# Revit family: Shower-Valves_and_Controls-KOHLER-Rite-Temp-K-8300
name_source: partatom
category: Plumbing Fixtures
revit_build: Autodesk Revit 2015 (Build: 20140606_1530(x64)
units: mm (PartAtom-declared; Revit-internal decimal feet)

## types (5) — shared parameters
ADA = No
Assembly Code = D2020
Cold Water Inlet = Cold Water Inlet
Date Modified = 09/20/2018
Default Elevation = 36"
Finish = Kohler-Metal-Brass
Flow Rate = 0 GPM
Height = 5 1/2"
Hot Water Inlet = Hot Water Inlet
Length = 3 1/2"
Manufacturer = KOHLER Co.
MasterFormat 1995 = 154300
MasterFormat 2004 = 22.11.00
Material = Brass Construction
Pressure = 0.00 psi
Product Documentation Link = http://www.us.kohler.com
Product Name = Rite-Temp
Product Page URL = http://www.us.kohler.com
Tempered Water Outlet 1 = Tempered Water Outlet 1
Tempered Water Outlet 2 = Tempered Water Outlet 2
URL = https://www.us.kohler.com
Waste Water Outlet = Waste Water Outlet

## per-type parameters (varying)
| type | Description | Model | Type | Width |
| K-Universal inlets | Valve body rough-in with universal inlets | K-8300-K-NA | 2 | 4 5/8" |
| KS-Service stops and universal inlets | Valve body rough-in with service stops and universal inlets | K-8300-KS-NA | 5 | 5 7/8" |
| PS-Service stops and PEX crimp connections | Valve body rough-in with service stops and PEX crimp connections | K-8300-PS-NA | 4 | 5 7/8" |
| PX-PEX crimp connections | Valve body rough-in with PEX crimp connections | K-8300-PX-NA | 3 | 4 9/16" |
| KSL-Service stops and universal inlets | Valve body rough-in with service stops (supplied loose) and universal inlets | K-8300-KS-NA | 1 | 5 7/8" |

## geometry (parser evidence)
native form markers: Blend x2, Sweep x5
no freeform markers — native parametric forms only
